# Revit family: Distanzmuffe sechskant
name_source: partatom
category: HLS-Bauteile
revit_build: Autodesk Revit 2017 (Build: 20190507_1515(x64)
units: mm (PartAtom-declared; Revit-internal decimal feet)

## family parameters
Arbeitsebenenbasiert = Nein
Beim Laden mit Abzugskörper schneiden = Nein
Bemaßung runder Anschluss = Durchmesser verwenden
Gemeinsam genutzt = Ja
Immer vertikal = Nein
Raumberechnungspunkt = Nein
Teiletyp = Normal

## types (4) — shared parameters
Fabrikat = MEFA
Firma = MEFA Befestigungs- und Montagesysteme GmbH
Kurztext1 = Distanzmuffe sechskant
Material = Stahl
Mengeneinheit = St
Oberflaeche = galvanisch verzinkt

## per-type parameters (varying)
| type | Artikelnummer | EAN | F2 | Gewicht | Gewicht pro Bauteil | H | Innengewinde 1 | Kurztext2 | Lochung | Länge | Länge Innengewinde 1 | Schlüsselweite | vpe |
| Distanzmuffe sechskant M 8 | 0700084 | 4250928416063 | 7 mm  [stored 0.0229659 ft] | 0.03 kg | 0.03 kg | 30 mm  [stored 0.0984252 ft] | M8 | Innengew. M8 L= 30 mm | 4 mm  [stored 0.0131234 ft] | 30 mm  [stored 0.0984252 ft] | 30 mm | 13 | 100 St |
| Distanzmuffe sechskant M10 | 0700104 | 4250928416087 | 9 mm | 0.06 kg | 0.06 kg | 40 mm  [stored 0.131234 ft] | M10 | Innengew. M10 L= 40 mm | 5 mm  [stored 0.0164042 ft] | 40 mm  [stored 0.131234 ft] | 40 mm | 17 | 50 St |
| Distanzmuffe sechskant M12 | 0700123 | 4250928449948 | 9 mm | 0.05 kg | 0.05 kg | 40 mm  [stored 0.131234 ft] | M12 | Innengew. M12 L= 40 mm | 6 mm  [stored 0.019685 ft] | 40 mm  [stored 0.131234 ft] | 40 mm | 17 | 50 St |
| Distanzmuffe sechskant M16 | 0700167 | 4250928416100 | 12 mm  [stored 0.0393701 ft] | 0.14 kg | 0.14 kg | 50 mm  [stored 0.164042 ft] | M16 | Innengew. M16 L= 50 mm | 8 mm  [stored 0.0262467 ft] | 50 mm  [stored 0.164042 ft] | 50 mm | 24 | 25 St |

note: [stored X ft] marks values corroborated as IEEE doubles in the binary element streams (Revit-internal decimal feet)

## geometry (parser evidence)
native form markers: Sweep x3
no freeform markers — native parametric forms only
